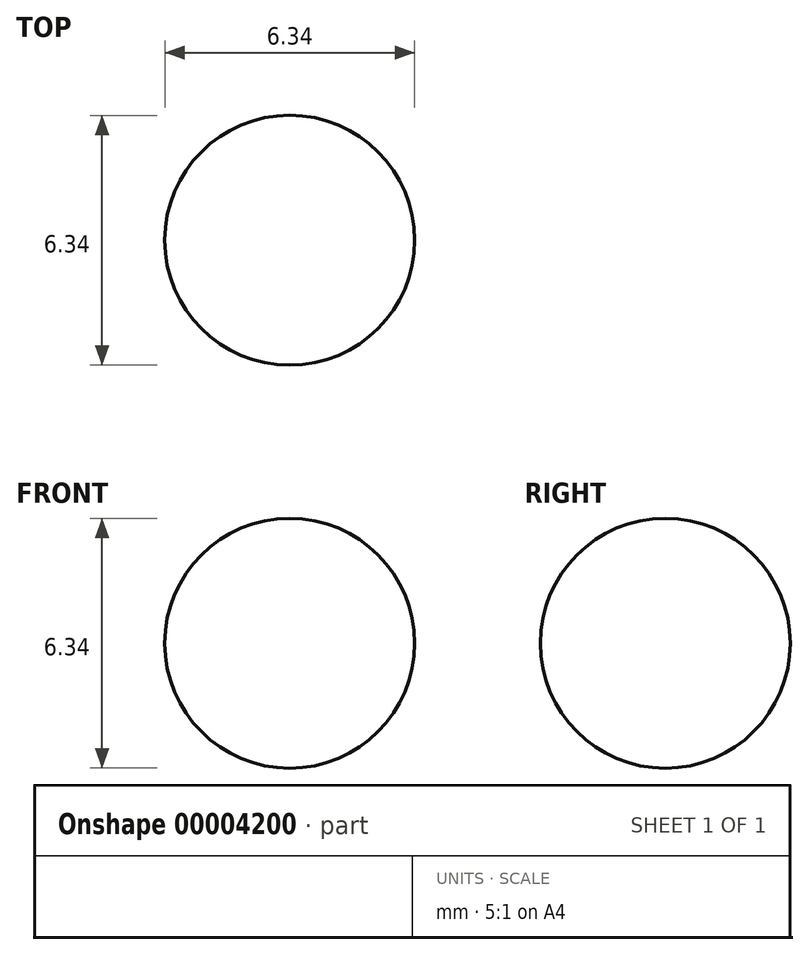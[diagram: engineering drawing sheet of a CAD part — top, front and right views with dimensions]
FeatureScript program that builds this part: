
annotation { "Feature Type Name" : "Feature", "Feature Type Description" : "" }
export const myFeature = defineFeature(function(context is Context, id is Id, definition is map)
    precondition{}
    {
        {
            var Q0;
            Q0=qCreatedBy(makeId("Front.planeOp"),FACE);
            var sketch = newSketch(context, id + "F0", { "sketchPlane" : qUnion([Q0])});
            skArc(sketch, "E0", {"start": v(0, 3.18) * mm, "mid": v(-3.18, 0) * mm, "end": v(0, -3.18) * mm});
            skLineSegment(sketch, "E1", {"start": v(0, 0) * mm, "end": v(0, 3.18) * mm, "construction": true});
            skLineSegment(sketch, "E2", {"start": v(0, 3.18) * mm, "end": v(0, -3.18) * mm});
            skSolve(sketch);
        }
        {
            var Q0;
            Q0=makeQuery(id+"F0.imprint","IMPRINT",FACE,{"disambiguationData":[TD([[makeQuery(id+"F0.imprint","IMPRINT",EDGE,{"derivedFrom":sQuery(id+"F0.wireOp",EDGE,"E0")}),1.0]])]});
            var Q1;
            Q1=sQuery(id+"F0.wireOp",EDGE,"E1");
            revolve(context, id + "F1", {"entities" : qUnion([Q0]), "axis" : qUnion([Q1]), "revolveType" : RevolveType.FULL});
        }
    });
